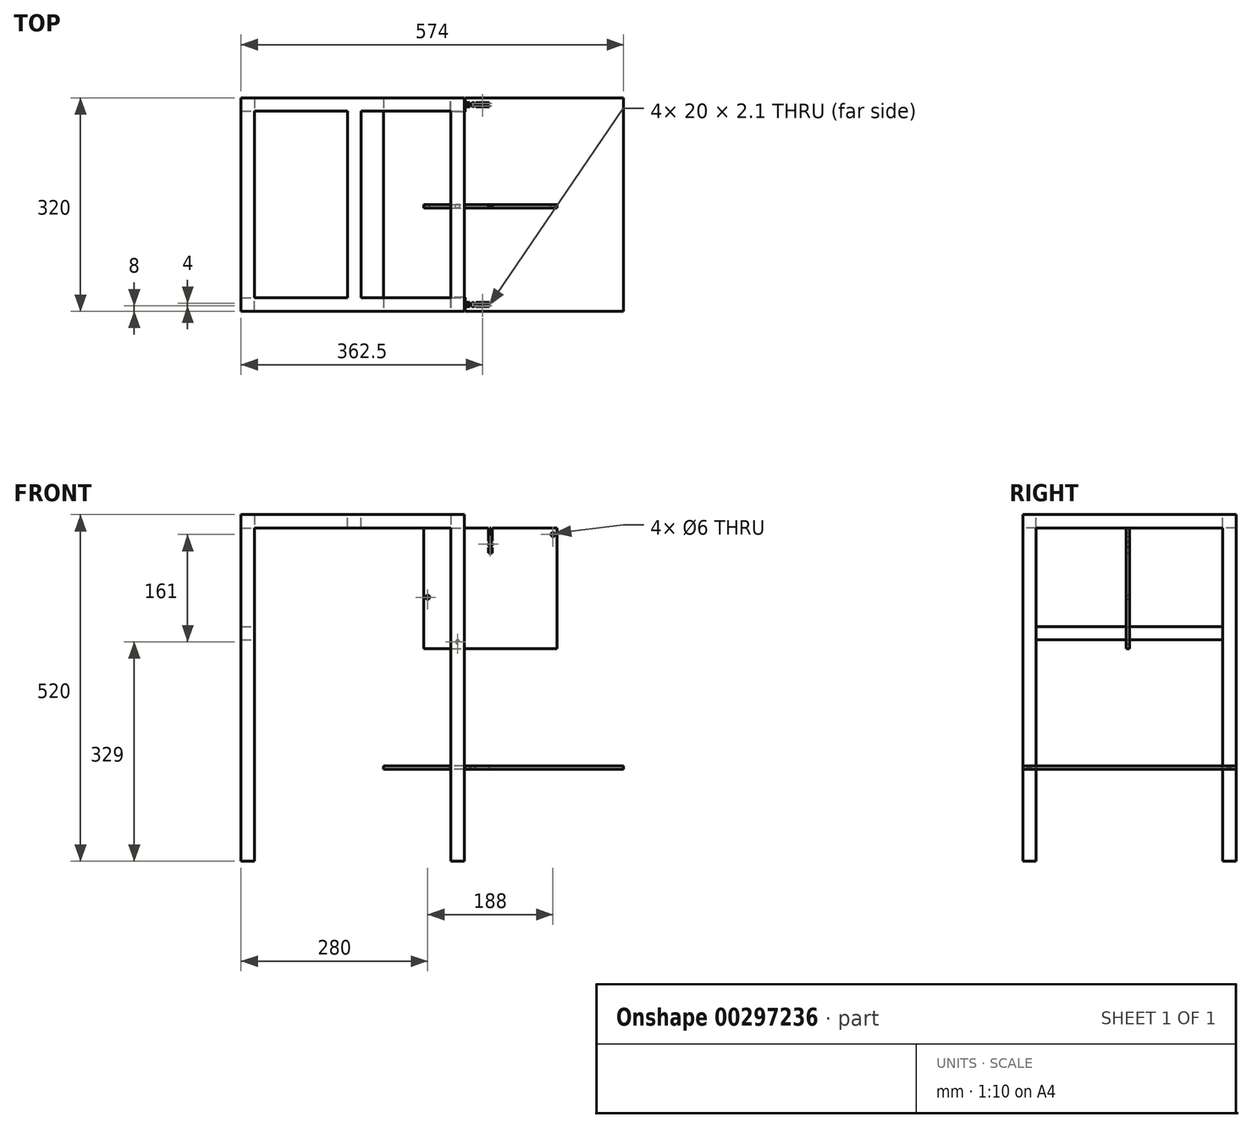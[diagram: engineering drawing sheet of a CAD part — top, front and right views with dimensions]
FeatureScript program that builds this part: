
annotation { "Feature Type Name" : "Feature", "Feature Type Description" : "" }
export const myFeature = defineFeature(function(context is Context, id is Id, definition is map)
    precondition{}
    {
        {
            var Q0;
            Q0=qCreatedBy(makeId("Front.planeOp"),FACE);
            var sketch = newSketch(context, id + "F0", { "sketchPlane" : qUnion([Q0])});
            skCircle(sketch, "E0", {"center": v(0, 0) * mm, "radius": 3 * mm});
            skCircle(sketch, "E1", {"center": v(-45, 67) * mm, "radius": 3 * mm});
            skCircle(sketch, "E2", {"center": v(143, 161) * mm, "radius": 3 * mm});
            skLineSegment(sketch, "E3.bottom", {"start": v(-51, -10) * mm, "end": v(149, -10) * mm});
            skLineSegment(sketch, "E3.top", {"start": v(-51, 171) * mm, "end": v(45.95, 171) * mm});
            skLineSegment(sketch, "E3.left", {"start": v(-51, -10) * mm, "end": v(-51, 171) * mm});
            skLineSegment(sketch, "E3.right", {"start": v(149, -10) * mm, "end": v(149, 171) * mm});
            skCircle(sketch, "E4", {"center": v(49, 146.5) * mm, "radius": 3 * mm});
            skPoint(sketch, "E4.centerSnap0", {"position": v(49, 171) * mm});
            skLineSegment(sketch, "E5.top", {"start": v(45.95, 151) * mm, "end": v(48.05, 151) * mm});
            skLineSegment(sketch, "E5.left", {"start": v(45.95, 171) * mm, "end": v(45.95, 151) * mm});
            skLineSegment(sketch, "E5.right", {"start": v(48.05, 171) * mm, "end": v(48.05, 151) * mm});
            skLineSegment(sketch, "E6.bottom", {"start": v(45.95, 141.5) * mm, "end": v(48.05, 141.5) * mm});
            skLineSegment(sketch, "E6.top", {"start": v(45.95, 133.5) * mm, "end": v(48.05, 133.5) * mm});
            skLineSegment(sketch, "E6.left", {"start": v(45.95, 141.5) * mm, "end": v(45.95, 133.5) * mm});
            skLineSegment(sketch, "E6.right", {"start": v(48.05, 141.5) * mm, "end": v(48.05, 133.5) * mm});
            skLineSegment(sketch, "E7.trimOffspring", {"start": v(48.05, 171) * mm, "end": v(149, 171) * mm});
            skLineSegment(sketch, "E8.MirrorCS", {"start": v(52.05, 133.5) * mm, "end": v(49.95, 133.5) * mm});
            skLineSegment(sketch, "E9.MirrorCS", {"start": v(52.05, 141.5) * mm, "end": v(49.95, 141.5) * mm});
            skLineSegment(sketch, "E10.MirrorCS", {"start": v(49.95, 171) * mm, "end": v(49.95, 151) * mm});
            skLineSegment(sketch, "E11.MirrorCS", {"start": v(52.05, 151) * mm, "end": v(49.95, 151) * mm});
            skLineSegment(sketch, "E12.MirrorCS", {"start": v(52.05, 141.5) * mm, "end": v(52.05, 133.5) * mm});
            skLineSegment(sketch, "E13.MirrorCS", {"start": v(49.95, 141.5) * mm, "end": v(49.95, 133.5) * mm});
            skLineSegment(sketch, "E14.MirrorCS", {"start": v(52.05, 171) * mm, "end": v(52.05, 151) * mm});
            skSolve(sketch);
        }
        {
            var Q0;
            Q0=makeQuery(id+"F0.imprint","IMPRINT",FACE,{"disambiguationData":[TD([[makeQuery(id+"F0.imprint","IMPRINT",EDGE,{"derivedFrom":sQuery(id+"F0.wireOp",EDGE,"E0")}),-1.0]])]});
            extrude(context, id + "F1", {"entities" : qUnion([Q0]), "depth" : 5 * mm});
        }
        {
            var Q0;
            Q0=qCreatedBy(makeId("Top.planeOp"),FACE);
            cPlane(context, id + "F2", {"entities" : qUnion([Q0]), "cplaneType" : CPlaneType.OFFSET, "offset" : 171 * mm, "width" : 150 * mm, "height" : 150 * mm});
        }
        {
            var Q0;
            Q0=qCreatedBy(id+"F2.planeOp",FACE);
            var sketch = newSketch(context, id + "F3", { "sketchPlane" : qUnion([Q0])});
            skLineSegment(sketch, "E15.bottom", {"start": v(10, -160) * mm, "end": v(-10, -160) * mm});
            skLineSegment(sketch, "E15.top", {"start": v(10, 160) * mm, "end": v(-10, 160) * mm});
            skLineSegment(sketch, "E15.left", {"start": v(10, -160) * mm, "end": v(10, 160) * mm});
            skLineSegment(sketch, "E15.right", {"start": v(-10, -160) * mm, "end": v(-10, 160) * mm});
            skLineSegment(sketch, "E16.bottom", {"start": v(-10, 160) * mm, "end": v(-305, 160) * mm});
            skLineSegment(sketch, "E16.top", {"start": v(-10, 140) * mm, "end": v(-305, 140) * mm});
            skLineSegment(sketch, "E16.left", {"start": v(-10, 160) * mm, "end": v(-10, 140) * mm});
            skLineSegment(sketch, "E16.right", {"start": v(-305, 160) * mm, "end": v(-305, 140) * mm});
            skLineSegment(sketch, "E17.bottom", {"start": v(-10, -160) * mm, "end": v(-305, -160) * mm});
            skLineSegment(sketch, "E17.top", {"start": v(-10, -140) * mm, "end": v(-305, -140) * mm});
            skLineSegment(sketch, "E17.left", {"start": v(-10, -160) * mm, "end": v(-10, -140) * mm});
            skLineSegment(sketch, "E17.right", {"start": v(-305, -160) * mm, "end": v(-305, -140) * mm});
            skLineSegment(sketch, "E18.bottom", {"start": v(-305, 160) * mm, "end": v(-325, 160) * mm});
            skLineSegment(sketch, "E18.top", {"start": v(-305, -160) * mm, "end": v(-325, -160) * mm});
            skLineSegment(sketch, "E18.left", {"start": v(-305, 160) * mm, "end": v(-305, -160) * mm});
            skLineSegment(sketch, "E18.right", {"start": v(-325, 160) * mm, "end": v(-325, -160) * mm});
            skSolve(sketch);
        }
        {
            var Q0;
            Q0=qSketchRegion(id+"F3",true);
            extrude(context, id + "F4", {"entities" : qUnion([Q0]), "operationType" : NewBodyOperationType.ADD, "depth" : 20 * mm});
        }
        {
            var Q0;
            Q0=makeQuery(id+"F4.opExtrude","CAP_FACE",FACE,{"disambiguationData":[OSD([sQuery(id+"F3.wireOp",EDGE,"E15.bottom"),sQuery(id+"F3.wireOp",EDGE,"E15.top"),sQuery(id+"F3.wireOp",EDGE,"E15.left"),sQuery(id+"F3.wireOp",EDGE,"E15.right"),sQuery(id+"F3.wireOp",EDGE,"7mnNWSTb-ftgJ-FYnv-rSfW-03W7qfMdHJeY.bottom"),sQuery(id+"F3.wireOp",EDGE,"7mnNWSTb-ftgJ-FYnv-rSfW-03W7qfMdHJeY.top"),sQuery(id+"F3.wireOp",EDGE,"yphk7Mg7-LXwZ-R6qe-Yzbn-fpSbBpRDTs4J.bottom"),sQuery(id+"F3.wireOp",EDGE,"yphk7Mg7-LXwZ-R6qe-Yzbn-fpSbBpRDTs4J.top"),sQuery(id+"F3.wireOp",EDGE,"yphk7Mg7-LXwZ-R6qe-Yzbn-fpSbBpRDTs4J.left"),sQuery(id+"F3.wireOp",EDGE,"yphk7Mg7-LXwZ-R6qe-Yzbn-fpSbBpRDTs4J.right"),sQuery(id+"F3.wireOp",EDGE,"9GNo11h2-buUj-PFzF-0UOW-2sDmyF7RkODV.bottom"),sQuery(id+"F3.wireOp",EDGE,"9GNo11h2-buUj-PFzF-0UOW-2sDmyF7RkODV.top")])],"isStart":true});
            var sketch = newSketch(context, id + "F5", { "sketchPlane" : qUnion([Q0])});
            skLineSegment(sketch, "E19.bottom", {"start": v(-325, 160) * mm, "end": v(-305, 160) * mm});
            skLineSegment(sketch, "E19.top", {"start": v(-325, 140) * mm, "end": v(-305, 140) * mm});
            skLineSegment(sketch, "E19.left", {"start": v(-325, 160) * mm, "end": v(-325, 140) * mm});
            skLineSegment(sketch, "E19.right", {"start": v(-305, 160) * mm, "end": v(-305, 140) * mm});
            skLineSegment(sketch, "E20.bottom", {"start": v(-325, -160) * mm, "end": v(-305, -160) * mm});
            skLineSegment(sketch, "E20.top", {"start": v(-325, -140) * mm, "end": v(-305, -140) * mm});
            skLineSegment(sketch, "E20.left", {"start": v(-325, -160) * mm, "end": v(-325, -140) * mm});
            skLineSegment(sketch, "E20.right", {"start": v(-305, -160) * mm, "end": v(-305, -140) * mm});
            skLineSegment(sketch, "E21.bottom", {"start": v(-10, -140) * mm, "end": v(10, -140) * mm});
            skLineSegment(sketch, "E21.top", {"start": v(-10, -160) * mm, "end": v(10, -160) * mm});
            skLineSegment(sketch, "E21.left", {"start": v(-10, -140) * mm, "end": v(-10, -160) * mm});
            skLineSegment(sketch, "E21.right", {"start": v(10, -140) * mm, "end": v(10, -160) * mm});
            skLineSegment(sketch, "E22.bottom", {"start": v(-10, 140) * mm, "end": v(10, 140) * mm});
            skLineSegment(sketch, "E22.top", {"start": v(-10, 160) * mm, "end": v(10, 160) * mm});
            skLineSegment(sketch, "E22.left", {"start": v(-10, 140) * mm, "end": v(-10, 160) * mm});
            skLineSegment(sketch, "E22.right", {"start": v(10, 140) * mm, "end": v(10, 160) * mm});
            skSolve(sketch);
        }
        {
            var Q0;
            Q0=qSketchRegion(id+"F5",true);
            extrude(context, id + "F6", {"entities" : qUnion([Q0]), "operationType" : NewBodyOperationType.ADD, "depth" : 500 * mm});
        }
        {
            var Q0;
            Q0=qCreatedBy(makeId("Top.planeOp"),FACE);
            cPlane(context, id + "F7", {"entities" : qUnion([Q0]), "cplaneType" : CPlaneType.OFFSET, "offset" : 186 * mm, "oppositeDirection" : true, "width" : 150 * mm, "height" : 150 * mm});
        }
        {
            var Q0;
            Q0=qCreatedBy(id+"F7.planeOp",FACE);
            var sketch = newSketch(context, id + "F8", { "sketchPlane" : qUnion([Q0])});
            skLineSegment(sketch, "E23.bottom", {"start": v(11, -139) * mm, "end": v(-11, -139) * mm});
            skPoint(sketch, "E23.middle", {"position": v(69, 0) * mm});
            skLineSegment(sketch, "E24.top", {"start": v(-111, 160) * mm, "end": v(-11, 160) * mm});
            skLineSegment(sketch, "E25.top", {"start": v(-111, -160) * mm, "end": v(-11, -160) * mm});
            skLineSegment(sketch, "E26.top", {"start": v(249, 160) * mm, "end": v(11, 160) * mm});
            skLineSegment(sketch, "E27.top", {"start": v(249, -160) * mm, "end": v(11, -160) * mm});
            skLineSegment(sketch, "E27.right", {"start": v(11, -139) * mm, "end": v(11, -146.95) * mm});
            skLineSegment(sketch, "E28", {"start": v(11, 160) * mm, "end": v(11, 153.05) * mm});
            skLineSegment(sketch, "E29", {"start": v(11, 139) * mm, "end": v(-11, 139) * mm});
            skLineSegment(sketch, "E30", {"start": v(-11, 139) * mm, "end": v(-11, 160) * mm});
            skCircle(sketch, "E31", {"center": v(23, 150) * mm, "radius": 3 * mm});
            skLineSegment(sketch, "E32.top", {"start": v(27.5, 153.05) * mm, "end": v(27.5, 150.95) * mm});
            skLineSegment(sketch, "E32.left", {"start": v(47.5, 153.05) * mm, "end": v(27.5, 153.05) * mm});
            skLineSegment(sketch, "E32.right", {"start": v(47.5, 150.95) * mm, "end": v(27.5, 150.95) * mm});
            skLineSegment(sketch, "E33.bottom", {"start": v(18, 153.05) * mm, "end": v(18, 150.95) * mm});
            skLineSegment(sketch, "E33.left", {"start": v(18, 153.05) * mm, "end": v(11, 153.05) * mm});
            skLineSegment(sketch, "E33.right", {"start": v(18, 150.95) * mm, "end": v(11, 150.95) * mm});
            skLineSegment(sketch, "E34.MirrorCS", {"start": v(18, 146.95) * mm, "end": v(18, 149.05) * mm});
            skLineSegment(sketch, "E35.MirrorCS", {"start": v(47.5, 149.05) * mm, "end": v(27.5, 149.05) * mm});
            skLineSegment(sketch, "E36.MirrorCS", {"start": v(27.5, 146.95) * mm, "end": v(27.5, 149.05) * mm});
            skLineSegment(sketch, "E37.MirrorCS", {"start": v(18, 146.95) * mm, "end": v(11, 146.95) * mm});
            skLineSegment(sketch, "E38.MirrorCS", {"start": v(18, 149.05) * mm, "end": v(11, 149.05) * mm});
            skLineSegment(sketch, "E39.MirrorCS", {"start": v(47.5, 146.95) * mm, "end": v(27.5, 146.95) * mm});
            skLineSegment(sketch, "E40", {"start": v(47.5, 146.95) * mm, "end": v(47.5, 149.05) * mm});
            skLineSegment(sketch, "E41", {"start": v(47.5, 150.95) * mm, "end": v(47.5, 153.05) * mm});
            skLineSegment(sketch, "E42.trimOffspring", {"start": v(11, 150.95) * mm, "end": v(11, 149.05) * mm});
            skLineSegment(sketch, "E43.trimOffspring", {"start": v(11, 146.95) * mm, "end": v(11, 139) * mm});
            skLineSegment(sketch, "E44", {"start": v(-11, -139) * mm, "end": v(-11, -160) * mm});
            skLineSegment(sketch, "E45", {"start": v(-111, 160) * mm, "end": v(-111, -160) * mm});
            skLineSegment(sketch, "E46", {"start": v(249, 160) * mm, "end": v(249, -160) * mm});
            skCircle(sketch, "E47", {"center": v(23, -150) * mm, "radius": 3 * mm});
            skLineSegment(sketch, "E48.top", {"start": v(27.5, -146.95) * mm, "end": v(27.5, -149.05) * mm});
            skLineSegment(sketch, "E48.left", {"start": v(47.5, -146.95) * mm, "end": v(27.5, -146.95) * mm});
            skLineSegment(sketch, "E48.right", {"start": v(47.5, -149.05) * mm, "end": v(27.5, -149.05) * mm});
            skLineSegment(sketch, "E49.bottom", {"start": v(18, -146.95) * mm, "end": v(18, -149.05) * mm});
            skLineSegment(sketch, "E49.left", {"start": v(18, -146.95) * mm, "end": v(11, -146.95) * mm});
            skLineSegment(sketch, "E49.right", {"start": v(18, -149.05) * mm, "end": v(11, -149.05) * mm});
            skLineSegment(sketch, "E50.MirrorCS", {"start": v(18, -153.05) * mm, "end": v(18, -150.95) * mm});
            skLineSegment(sketch, "E51.MirrorCS", {"start": v(47.5, -150.95) * mm, "end": v(27.5, -150.95) * mm});
            skLineSegment(sketch, "E52.MirrorCS", {"start": v(27.5, -153.05) * mm, "end": v(27.5, -150.95) * mm});
            skLineSegment(sketch, "E53.MirrorCS", {"start": v(18, -153.05) * mm, "end": v(11, -153.05) * mm});
            skLineSegment(sketch, "E54.MirrorCS", {"start": v(18, -150.95) * mm, "end": v(11, -150.95) * mm});
            skLineSegment(sketch, "E55.MirrorCS", {"start": v(47.5, -153.05) * mm, "end": v(27.5, -153.05) * mm});
            skLineSegment(sketch, "E56", {"start": v(47.5, -153.05) * mm, "end": v(47.5, -150.95) * mm});
            skLineSegment(sketch, "E57", {"start": v(47.5, -149.05) * mm, "end": v(47.5, -146.95) * mm});
            skLineSegment(sketch, "E58.trimOffspring", {"start": v(11, -149.05) * mm, "end": v(11, -150.95) * mm});
            skLineSegment(sketch, "E59.trimOffspring", {"start": v(11, -153.05) * mm, "end": v(11, -160) * mm});
            skLineSegment(sketch, "E60", {"start": v(0, 0) * mm, "end": v(0, 174.93) * mm});
            skSolve(sketch);
        }
        {
            var Q0;
            Q0=makeQuery(id+"F8.imprint","IMPRINT",FACE,{"disambiguationData":[TD([[makeQuery(id+"F8.imprint","IMPRINT",EDGE,{"derivedFrom":sQuery(id+"F8.wireOp",EDGE,"E23.bottom")}),-1.0]])]});
            extrude(context, id + "F9", {"entities" : qUnion([Q0]), "operationType" : NewBodyOperationType.ADD, "oppositeDirection" : true, "depth" : 5 * mm});
        }
        {
            var Q0;
            Q0=makeQuery(id+"F6.opExtrude","SWEPT_FACE",FACE,{"disambiguationData":[OSD([sQuery(id+"F5.wireOp",EDGE,"E20.top")])]});
            var sketch = newSketch(context, id + "F10", { "sketchPlane" : qUnion([Q0])});
            skLineSegment(sketch, "E61.bottom", {"start": v(-325, 3) * mm, "end": v(-305, 3) * mm});
            skLineSegment(sketch, "E61.top", {"start": v(-325, 23) * mm, "end": v(-305, 23) * mm});
            skLineSegment(sketch, "E61.left", {"start": v(-325, 3) * mm, "end": v(-325, 23) * mm});
            skLineSegment(sketch, "E61.right", {"start": v(-305, 3) * mm, "end": v(-305, 23) * mm});
            skSolve(sketch);
        }
        {
            var Q0;
            Q0=qSketchRegion(id+"F10",true);
            extrude(context, id + "F11", {"entities" : qUnion([Q0]), "operationType" : NewBodyOperationType.ADD, "depth" : 280 * mm});
        }
        {
            var Q0;
            Q0=makeQuery(id+"F4.opExtrude","SWEPT_FACE",FACE,{"disambiguationData":[OSD([sQuery(id+"F3.wireOp",EDGE,"E16.top")])]});
            var sketch = newSketch(context, id + "F12", { "sketchPlane" : qUnion([Q0])});
            skLineSegment(sketch, "E62.bottom", {"start": v(-165, 171) * mm, "end": v(-145, 171) * mm});
            skLineSegment(sketch, "E62.top", {"start": v(-165, 191) * mm, "end": v(-145, 191) * mm});
            skLineSegment(sketch, "E62.left", {"start": v(-165, 171) * mm, "end": v(-165, 191) * mm});
            skLineSegment(sketch, "E62.right", {"start": v(-145, 171) * mm, "end": v(-145, 191) * mm});
            skSolve(sketch);
        }
        {
            var Q0;
            Q0=makeQuery(id+"F12.imprint","IMPRINT",FACE,{"disambiguationData":[TD([[makeQuery(id+"F12.imprint","IMPRINT",EDGE,{"derivedFrom":sQuery(id+"F12.wireOp",EDGE,"E62.bottom")}),-1.0]])]});
            extrude(context, id + "F13", {"entities" : qUnion([Q0]), "operationType" : NewBodyOperationType.ADD, "depth" : 280 * mm});
        }
    });
